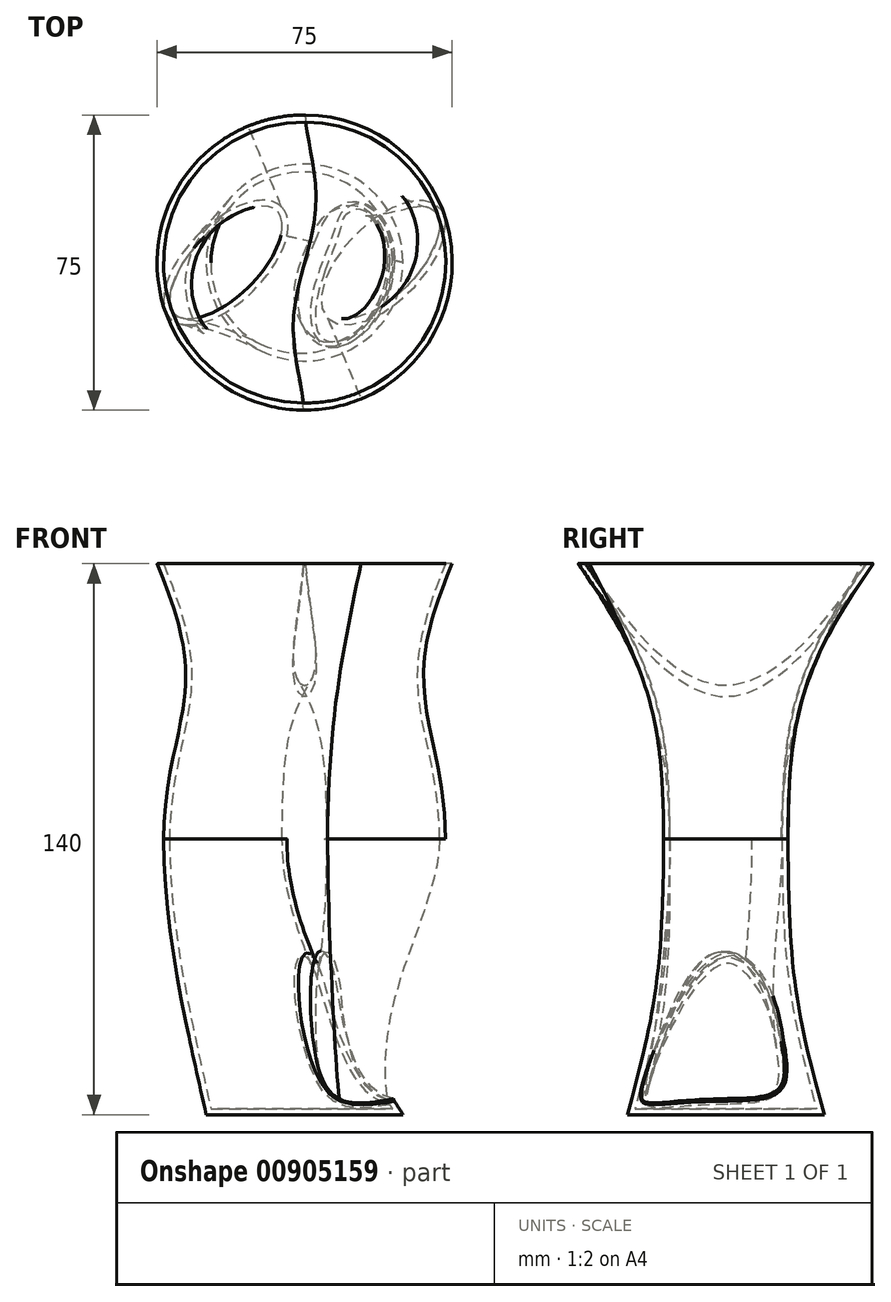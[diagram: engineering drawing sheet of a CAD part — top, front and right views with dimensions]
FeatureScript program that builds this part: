
annotation { "Feature Type Name" : "Feature", "Feature Type Description" : "" }
export const myFeature = defineFeature(function(context is Context, id is Id, definition is map)
    precondition{}
    {
        {
            var Q0;
            Q0=qCreatedBy(makeId("Top.planeOp"),FACE);
            var sketch = newSketch(context, id + "F0", { "sketchPlane" : qUnion([Q0])});
            skEllipse(sketch, "E0", {"center": v(0, 0) * mm, "majorRadius": 20 * mm, "minorRadius": 10 * mm, "majorAxis": v(0.7, 0.7)});
            skLineSegment(sketch, "E1", {"start": v(0, 0) * mm, "end": v(14.14, 14.14) * mm, "construction": true});
            skSolve(sketch);
        }
        {
            var Q0;
            Q0=qCreatedBy(makeId("Top.planeOp"),FACE);
            cPlane(context, id + "F1", {"entities" : qUnion([Q0]), "cplaneType" : CPlaneType.OFFSET, "offset" : 70 * mm, "width" : 150 * mm, "height" : 150 * mm});
        }
        {
            var Q0;
            Q0=qCreatedBy(id+"F1.planeOp",FACE);
            var sketch = newSketch(context, id + "F2", { "sketchPlane" : qUnion([Q0])});
            skCircle(sketch, "E2", {"center": v(20, 0) * mm, "radius": 37.5 * mm});
            skSolve(sketch);
        }
        {
            var Q0;
            Q0=makeQuery(id+"F0.imprint","IMPRINT",FACE,{"disambiguationData":[TD([[makeQuery(id+"F0.imprint","IMPRINT",EDGE,{"derivedFrom":sQuery(id+"F0.wireOp",EDGE,"E0")}),1.0]])]});
            var Q1;
            Q1=makeQuery(id+"F2.imprint","IMPRINT",FACE,{"disambiguationData":[TD([[makeQuery(id+"F2.imprint","IMPRINT",EDGE,{"derivedFrom":sQuery(id+"F2.wireOp",EDGE,"E2")}),1.0]])]});
            loft(context, id + "F3", {"startCondition" : LoftEndDerivativeType.NORMAL_TO_PROFILE, "startMagnitude" : 1.3, "sheetProfilesArray" : [{ "sheetProfileEntities" : qUnion([Q0]) }, { "sheetProfileEntities" : qUnion([Q1]) }]});
        }
        {
            var Q0;
            Q0=qCreatedBy(makeId("Top.planeOp"),FACE);
            var sketch = newSketch(context, id + "F4", { "sketchPlane" : qUnion([Q0])});
            skEllipse(sketch, "E3", {"center": v(40, 0) * mm, "majorRadius": 20 * mm, "minorRadius": 10 * mm, "majorAxis": v(-0.7, -0.7)});
            skLineSegment(sketch, "E4", {"start": v(40, 0) * mm, "end": v(25.86, -14.14) * mm, "construction": true});
            skSolve(sketch);
        }
        {
            var Q1;
            Q1=makeQuery(id+"F4.imprint","IMPRINT",FACE,{"disambiguationData":[TD([[makeQuery(id+"F4.imprint","IMPRINT",EDGE,{"derivedFrom":sQuery(id+"F4.wireOp",EDGE,"E3")}),1.0]])]});
            var Q2;
            Q2=makeQuery(id+"F3.opLoft","CAP_FACE",FACE,{"disambiguationData":[OSD([makeQuery(id+"F2.imprint","IMPRINT",FACE,{"disambiguationData":[TD([[makeQuery(id+"F2.imprint","IMPRINT",EDGE,{"derivedFrom":sQuery(id+"F2.wireOp",EDGE,"E2")}),1.0]])]})])],"isStart":true});
            loft(context, id + "F5", {"operationType" : NewBodyOperationType.ADD, "startCondition" : LoftEndDerivativeType.NORMAL_TO_PROFILE, "startMagnitude" : 1.3, "sheetProfilesArray" : [{ "sheetProfileEntities" : qUnion([Q1]) }, { "sheetProfileEntities" : qUnion([Q2]) }]});
        }
        {
            var Q0;
            Q0=qCreatedBy(makeId("Top.planeOp"),FACE);
            cPlane(context, id + "F6", {"entities" : qUnion([Q0]), "cplaneType" : CPlaneType.OFFSET, "offset" : 70 * mm, "oppositeDirection" : true, "width" : 150 * mm, "height" : 150 * mm});
        }
        {
            var Q0;
            Q0=qCreatedBy(id+"F6.planeOp",FACE);
            var sketch = newSketch(context, id + "F7", { "sketchPlane" : qUnion([Q0])});
            skCircle(sketch, "E5", {"center": v(20, 0) * mm, "radius": 25 * mm});
            skSolve(sketch);
        }
        {
            var Q1;
            Q1=makeQuery(id+"F7.imprint","IMPRINT",FACE,{"disambiguationData":[TD([[makeQuery(id+"F7.imprint","IMPRINT",EDGE,{"derivedFrom":sQuery(id+"F7.wireOp",EDGE,"E5")}),1.0]])]});
            var Q2;
            Q2=makeQuery(id+"F3.opLoft","CAP_FACE",FACE,{"disambiguationData":[OSD([makeQuery(id+"F0.imprint","IMPRINT",FACE,{"disambiguationData":[TD([[makeQuery(id+"F0.imprint","IMPRINT",EDGE,{"derivedFrom":sQuery(id+"F0.wireOp",EDGE,"E0")}),1.0]])]})])],"isStart":true});
            loft(context, id + "F8", {"operationType" : NewBodyOperationType.ADD, "endCondition" : LoftEndDerivativeType.NORMAL_TO_PROFILE, "endMagnitude" : 1, "sheetProfilesArray" : [{ "sheetProfileEntities" : qUnion([Q1]) }, { "sheetProfileEntities" : qUnion([Q2]) }]});
        }
        {
            var Q1;
            Q1=makeQuery(id+"F5.opLoft","CAP_FACE",FACE,{"disambiguationData":[OSD([makeQuery(id+"F4.imprint","IMPRINT",FACE,{"disambiguationData":[TD([[makeQuery(id+"F4.imprint","IMPRINT",EDGE,{"derivedFrom":sQuery(id+"F4.wireOp",EDGE,"E3")}),1.0]])]})])],"isStart":true});
            var Q2;
            Q2=makeQuery(id+"F8.opLoft","CAP_FACE",FACE,{"disambiguationData":[OSD([makeQuery(id+"F7.imprint","IMPRINT",FACE,{"disambiguationData":[TD([[makeQuery(id+"F7.imprint","IMPRINT",EDGE,{"derivedFrom":sQuery(id+"F7.wireOp",EDGE,"E5")}),1.0]])]})])],"isStart":true});
            loft(context, id + "F9", {"operationType" : NewBodyOperationType.ADD, "startCondition" : LoftEndDerivativeType.NORMAL_TO_PROFILE, "startMagnitude" : 1, "endCondition" : LoftEndDerivativeType.TANGENT_TO_PROFILE, "endMagnitude" : 1, "sheetProfilesArray" : [{ "sheetProfileEntities" : qUnion([Q1]) }, { "sheetProfileEntities" : qUnion([Q2]) }]});
        }
        {
            var Q0;
            {var subQ0=sQuery(id+"F7.wireOp",EDGE,"E5");Q0=makeQuery(id+"F9.boolean.opBoolean","INTERSECT",EDGE,{"derivedFrom":[makeQuery(id+"F8.opLoft","SWEPT_FACE",FACE,{"disambiguationData":[OSD([sQuery(id+"F0.wireOp",EDGE,"E0"),subQ0])]}),makeQuery(id+"F9.opLoft","SWEPT_FACE",FACE,{"disambiguationData":[OSD([sQuery(id+"F4.wireOp",EDGE,"E3"),subQ0])]})]});}
            fillet(context, id + "F10", {"entities" : qUnion([Q0]), "radius" : 2 * mm, "tangentPropagation" : true, "allowEdgeOverflow" : false});
        }
        {
            var Q0;
            {var subQ0=sQuery(id+"F2.wireOp",EDGE,"E2");var subQ1=makeQuery(id+"F3.opLoft","SWEPT_FACE",FACE,{"disambiguationData":[OSD([sQuery(id+"F0.wireOp",EDGE,"E0"),subQ0])]});var subQ2=makeQuery(id+"F5.opLoft","SWEPT_FACE",FACE,{"disambiguationData":[OSD([subQ0,sQuery(id+"F4.wireOp",EDGE,"E3")])]});Q0=makeQuery(id+"F5.boolean.opBoolean","INTERSECT",EDGE,{"disambiguationData":[topologyDisambiguationEdgeConnected([subQ1,subQ2]),OD(1.0)],"derivedFrom":[subQ1,subQ2]});}
            fillet(context, id + "F11", {"entities" : qUnion([Q0]), "radius" : 2 * mm, "tangentPropagation" : true, "allowEdgeOverflow" : false});
        }
        {
            var Q0;
            Q0=makeQuery(id+"F3.opLoft","CAP_FACE",FACE,{"disambiguationData":[OSD([makeQuery(id+"F2.imprint","IMPRINT",FACE,{"disambiguationData":[TD([[makeQuery(id+"F2.imprint","IMPRINT",EDGE,{"derivedFrom":sQuery(id+"F2.wireOp",EDGE,"E2")}),1.0]])]})])],"isStart":true});
            shell(context, id + "F12", {"entities" : qUnion([Q0]), "thickness" : 1.5 * mm});
        }
    });
